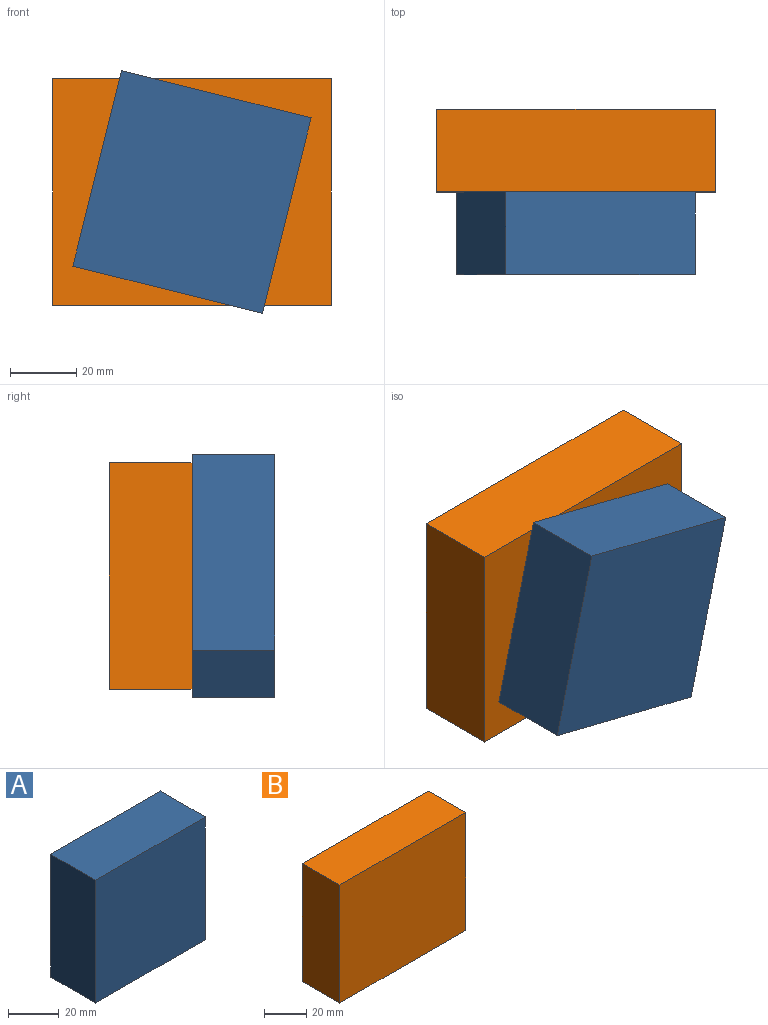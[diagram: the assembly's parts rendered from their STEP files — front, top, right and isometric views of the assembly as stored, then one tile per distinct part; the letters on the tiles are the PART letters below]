
ASSEMBLY  parts=2 mates=1
PART A: 6 faces, bbox 61x25x59.2 mm
  f0: plane 59.16x25mm, normal (-1,0,0), area 1478.9mm2, adj f1,f3,f4,f5
  f1: plane 61.02x25mm, normal (0,0,-1), area 1525.4mm2, adj f0,f2,f4,f5
  f2: plane 59.16x25mm, normal (1,0,0), area 1478.9mm2, adj f1,f3,f4,f5
  f3: plane 61.02x25mm, normal (0,0,1), area 1525.4mm2, adj f0,f2,f4,f5
  f4: plane 61.02x59.16mm, normal (0,-1,0), area 3609.6mm2, adj f0,f1,f2,f3
  f5: plane 61.02x59.16mm, normal (0,1,0), area 3609.6mm2, adj f0,f1,f2,f3
PART B: 6 faces, bbox 84.4x25x68.5 mm
  f0: plane 68.5x25mm, normal (-1,0,0), area 1712.5mm2, adj f1,f3,f4,f5
  f1: plane 84.39x25mm, normal (0,0,-1), area 2109.6mm2, adj f0,f2,f4,f5
  f2: plane 68.5x25mm, normal (1,0,0), area 1712.5mm2, adj f1,f3,f4,f5
  f3: plane 84.39x25mm, normal (0,0,1), area 2109.6mm2, adj f0,f2,f4,f5
  f4: plane 84.39x68.5mm, normal (0,-1,0), area 5780.4mm2, adj f0,f1,f2,f3
  f5: plane 84.39x68.5mm, normal (0,1,0), area 5780.4mm2, adj f0,f1,f2,f3
PLACE A rot(axis=(0.62,0,-0.79),180deg) t=(82.56,-50,-78)mm
PLACE B at identity fixed
MATE revolute A.f4 <-> B.f4  axis (0,1,0) through (95.26,-25,15)mm
